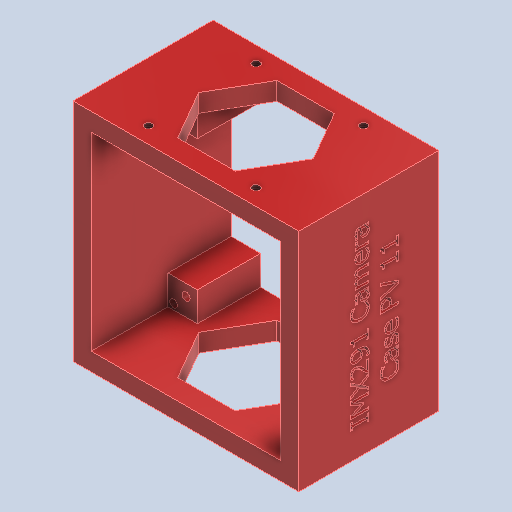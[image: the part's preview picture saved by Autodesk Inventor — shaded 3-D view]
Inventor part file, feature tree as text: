
AUTODESK INVENTOR PART (.ipt)
format: ipt  version: 2023 (Build 270158030, 158C)  size: 897,536 bytes
history: native  units: mm
features: sketch x6, extrude x3, other x2, hole x2, emboss x1
ambient origin geometry x8: Origin, YZ Plane, XZ Plane, XY Plane, X Axis, Y Axis, Z Axis, Center Point
bodies: Solid5 (feature_tree)
feature tree (14):
  other  "Annotations"
  extrude  "Extrusion9"  Depth=34.0mm
  extrude  "Extrusion10"  Depth=42.0mm
  emboss  "Emboss2"
  hole  "Hole1"  [1 undecoded]
  sketch  "Sketch14"  dims[d54=29.0mm d55=14.0mm d56=0.0mm]
  hole  "Hole3"  [1 undecoded]
  extrude  "Extrusion13"  Depth=14.0mm TaperAngle=0.0deg
  sketch  "Sketch8"  dims[d46=34.0mm d47=34.0mm]
  sketch  "Sketch9"  dims[d48=1.8mm d49=42.0mm]
  sketch  "Sketch10"  dims[d50=42.0mm d51=4.0mm]
  sketch  "Sketch11"  dims[d52=4.0mm d53=29.0mm]
  sketch  "Sketch15"  dims[d57=17.0mm d58=0.0mm d59=1.0mm d60=0.0mm d61=50.0mm d62=50.0mm d65=1.69418mm d66=4.369mm d67=4.0mm d68=2.0mm d69=90.0deg d70=8.0mm d71=20.594885mm d74=39.5mm d75=39.5mm d93=23.8mm d94=1.69418mm d95=4.369mm d96=4.0mm d97=2.0mm d98=90.0deg d99=8.0mm d100=0.0mm d101=22.0mm d102=0.0mm d103=0.0mm d76=1.606368mm d77=5.419804mm d78=14.0mm d79=0.5mm d80=0.872665mm d81=0.5mm d82=0.872665mm]
  other  "Linear Dimension 1"
note: 2 required parameter values undecoded (feature->parameter linkage not recoverable at this tier; creation-order binding heuristic only, values carry confidence <= 0.55)
